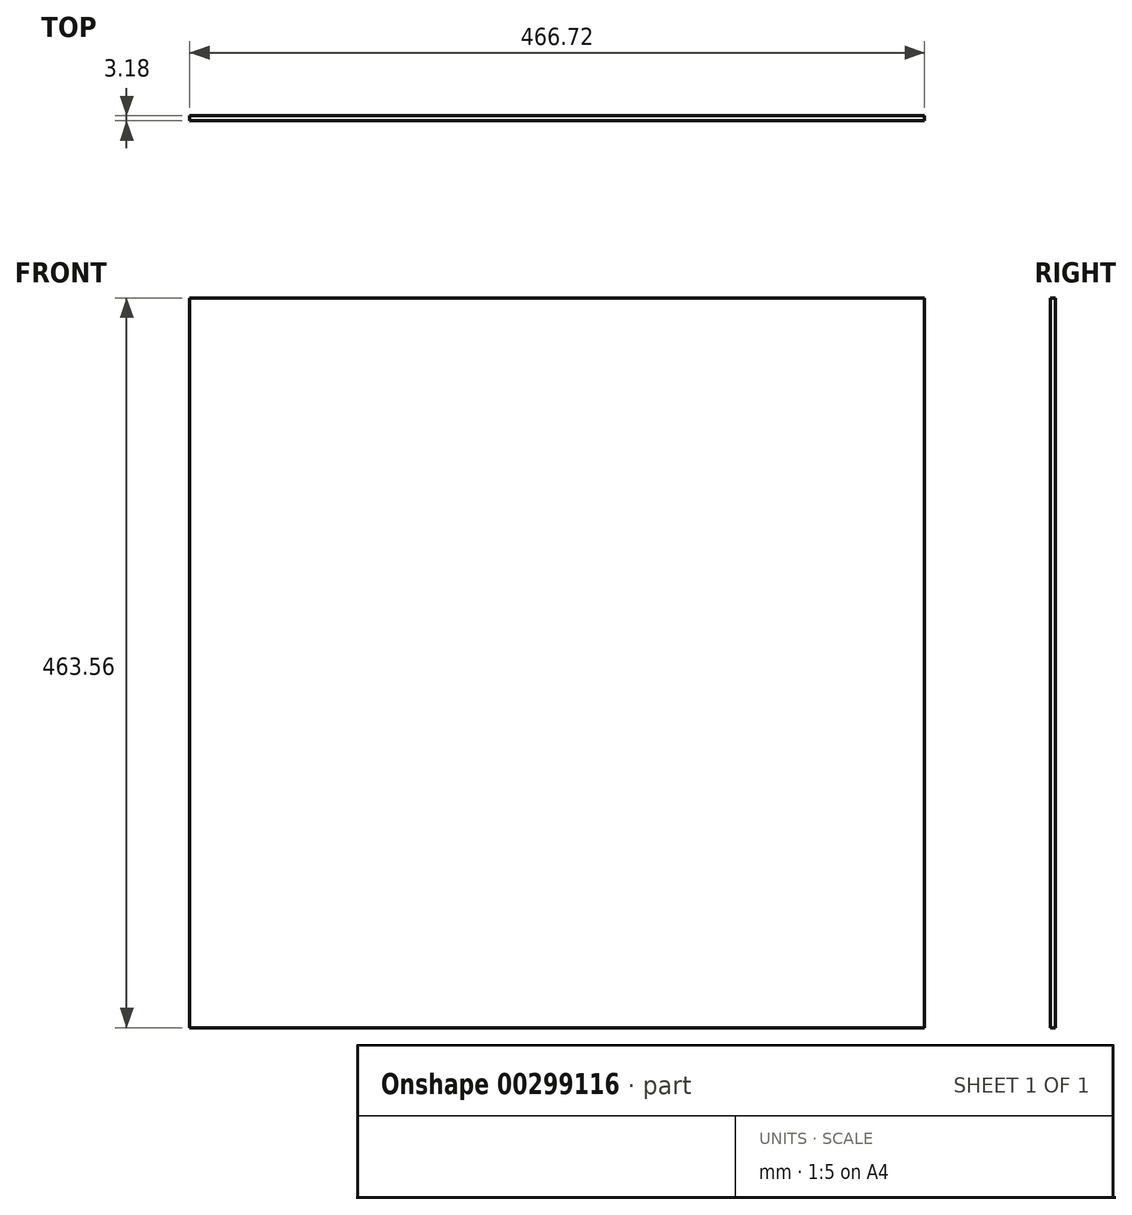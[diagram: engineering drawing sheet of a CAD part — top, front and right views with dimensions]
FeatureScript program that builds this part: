
annotation { "Feature Type Name" : "Feature", "Feature Type Description" : "" }
export const myFeature = defineFeature(function(context is Context, id is Id, definition is map)
    precondition{}
    {
        {
            var Q0;
            Q0=qCreatedBy(makeId("Top.planeOp"),FACE);
            var sketch = newSketch(context, id + "F0", { "sketchPlane" : qUnion([Q0])});
            skLineSegment(sketch, "E0.bottom", {"start": v(233.36, 1.59) * mm, "end": v(-233.36, 1.59) * mm});
            skLineSegment(sketch, "E0.top", {"start": v(233.36, -1.59) * mm, "end": v(-233.36, -1.59) * mm});
            skLineSegment(sketch, "E0.left", {"start": v(233.36, 1.59) * mm, "end": v(233.36, -1.59) * mm});
            skLineSegment(sketch, "E0.right", {"start": v(-233.36, 1.59) * mm, "end": v(-233.36, -1.59) * mm});
            skPoint(sketch, "E0.middle", {"position": v(0, 0) * mm});
            skSolve(sketch);
        }
        {
            var Q0;
            Q0 = qSketchRegion(id + "F0", true);
            extrude(context, id + "F1", {"entities" : qUnion([Q0]), "endBound" : BoundingType.SYMMETRIC, "depth" : 463.55 * mm});
        }
    });
